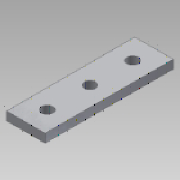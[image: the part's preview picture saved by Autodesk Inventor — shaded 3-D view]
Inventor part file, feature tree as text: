
AUTODESK INVENTOR PART (.ipt)
format: ipt  version: 2013 (Build 170138000, 138)  size: 100,352 bytes
history: native  units: mm
features: extrude x1, sketch x1
ambient origin geometry x8: Origin, YZ Plane, XZ Plane, XY Plane, X Axis, Y Axis, Z Axis, Center Point
bodies: Solid1 (feature_tree)
feature tree (2):
  extrude  "Extrusion1"  Depth=60.0mm
  sketch  "Sketch1"  dims[d0=18.0mm d2=60.0mm d3=5.3mm d4=5.3mm d5=20.0mm d6=9.0mm d7=5.3mm d8=20.0mm d9=9.0mm d10=4.0mm d11=0.0mm]
